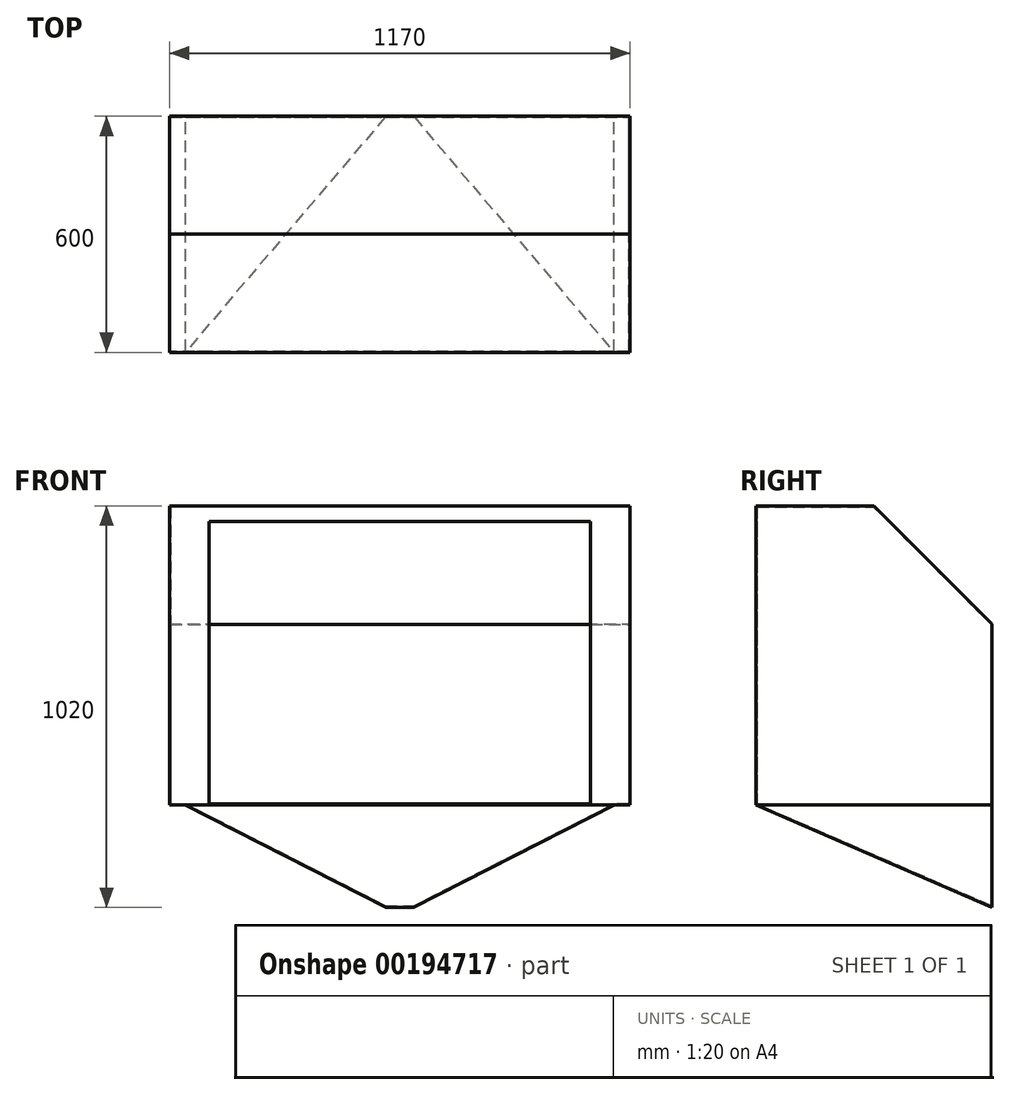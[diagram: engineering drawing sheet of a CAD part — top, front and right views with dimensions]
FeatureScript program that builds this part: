
annotation { "Feature Type Name" : "Feature", "Feature Type Description" : "" }
export const myFeature = defineFeature(function(context is Context, id is Id, definition is map)
    precondition{}
    {
        {
            var Q0;
            Q0=qCreatedBy(makeId("Right.planeOp"),FACE);
            var sketch = newSketch(context, id + "F0", { "sketchPlane" : qUnion([Q0])});
            skLineSegment(sketch, "E0.bottom", {"start": v(-4.06, 760) * mm, "end": v(295.94, 760) * mm});
            skLineSegment(sketch, "E0.top", {"start": v(-4.06, 0) * mm, "end": v(595.94, 0) * mm});
            skLineSegment(sketch, "E0.left", {"start": v(-4.06, 760) * mm, "end": v(-4.06, 0) * mm});
            skLineSegment(sketch, "E0.right", {"start": v(595.94, 460) * mm, "end": v(595.94, 0) * mm});
            skLineSegment(sketch, "E1", {"start": v(295.94, 760) * mm, "end": v(595.94, 460) * mm});
            skLineSegment(sketch, "E2", {"start": v(-4.06, 0) * mm, "end": v(595.94, -260) * mm});
            skLineSegment(sketch, "E3", {"start": v(595.94, -260) * mm, "end": v(595.94, 0) * mm});
            skSolve(sketch);
        }
        {
            var Q0;
            Q0=makeQuery(id+"F0.imprint","IMPRINT",FACE,{"disambiguationData":[TD([[makeQuery(id+"F0.imprint","IMPRINT",EDGE,{"derivedFrom":sQuery(id+"F0.wireOp",EDGE,"E0.bottom")}),-1.0]])]});
            var Q1;
            Q1=makeQuery(id+"F0.imprint","IMPRINT",FACE,{"disambiguationData":[TD([[makeQuery(id+"F0.imprint","IMPRINT",EDGE,{"derivedFrom":sQuery(id+"F0.wireOp",EDGE,"E0.top")}),-1.0]])]});
            extrude(context, id + "F1", {"entities" : qUnion([Q0, Q1]), "oppositeDirection" : true, "depth" : 1170 * mm, "symmetric" : true});
        }
        {
            var Q0;
            {var subQ0=sQuery(id+"F0.wireOp",EDGE,"E3");var subQ2=sQuery(id+"F0.wireOp",EDGE,"E1");var subQ3=sQuery(id+"F0.wireOp",EDGE,"E0.right");Q0=makeQuery(id+"FbMwOEGK0U6XBFF_1.boolean.opBoolean","SPLIT",FACE,{"disambiguationData":[TD([makeQuery(id+"F1.opExtrude","SWEPT_FACE",FACE,{"disambiguationData":[OSD([subQ2])]})])],"derivedFrom":makeQuery(id+"F1.opExtrude","SWEPT_FACE",FACE,{"disambiguationData":[OSD([subQ3,subQ0])]})});}
            var sketch = newSketch(context, id + "F2", { "sketchPlane" : qUnion([Q0])});
            skLineSegment(sketch, "E4", {"start": v(-585, 0) * mm, "end": v(-585, -260) * mm});
            skLineSegment(sketch, "E5", {"start": v(-585, -260) * mm, "end": v(-35, -260) * mm});
            skLineSegment(sketch, "E6", {"start": v(585, -260) * mm, "end": v(585, 0) * mm});
            skLineSegment(sketch, "E7", {"start": v(35, -260) * mm, "end": v(585, -260) * mm});
            skLineSegment(sketch, "E8", {"start": v(-585, 0) * mm, "end": v(-545, 0) * mm});
            skLineSegment(sketch, "E9", {"start": v(-545, 0) * mm, "end": v(-35, -260) * mm});
            skLineSegment(sketch, "E10", {"start": v(585, 0) * mm, "end": v(545, 0) * mm});
            skLineSegment(sketch, "E11", {"start": v(545, 0) * mm, "end": v(35, -260) * mm});
            skSolve(sketch);
        }
        {
            var Q0;
            Q0=makeQuery(id+"F2.imprint","IMPRINT",FACE,{"disambiguationData":[TD([[makeQuery(id+"F2.imprint","IMPRINT",EDGE,{"derivedFrom":sQuery(id+"F2.wireOp",EDGE,"E4")}),1.0]])]});
            var Q1;
            Q1=makeQuery(id+"F2.imprint","IMPRINT",FACE,{"disambiguationData":[TD([[makeQuery(id+"F2.imprint","IMPRINT",EDGE,{"derivedFrom":sQuery(id+"F2.wireOp",EDGE,"E6")}),-1.0]])]});
            extrude(context, id + "F3", {"entities" : qUnion([Q0, Q1]), "operationType" : NewBodyOperationType.REMOVE, "endBound" : BoundingType.THROUGH_ALL, "oppositeDirection" : true, "depth" : 25 * mm});
        }
        {
            var Q0;
            Q0=makeQuery(id+"F1.opExtrude","SWEPT_FACE",FACE,{"disambiguationData":[OSD([sQuery(id+"F0.wireOp",EDGE,"E0.left")])]});
            shell(context, id + "F4", {"entities" : qUnion([Q0]), "thickness" : 2.5 * mm});
        }
        {
            var Q0;
            {var subQ0=makeQuery(id+"F1.opExtrude","SWEPT_FACE",FACE,{"disambiguationData":[OSD([sQuery(id+"F0.wireOp",EDGE,"E0.right")])]});Q0=makeQuery(id+"FFsGgMnDsrMl6fX_1.boolean.opBoolean","MERGE",FACE,{"derivedFrom":[subQ0,makeQuery(id+"F2FXjvtt2T8WuFh_2.opPattern","COPY",FACE,{"derivedFrom":subQ0,"instanceName":"1"}),makeQuery(id+"FFsGgMnDsrMl6fX_1.opExtrude","SWEPT_FACE",FACE,{"disambiguationData":[OSD([sQuery(id+"FZ7NtepqDCPp275_1.wireOp",EDGE,"sU0Ndzhe-5L0x-tQlU-vsOd-fbsLByKIB5Rt")])]})]});}
            var sketch = newSketch(context, id + "F5", { "sketchPlane" : qUnion([Q0])});
            skCircle(sketch, "E12", {"center": v(0, -175) * mm, "radius": 80 * mm});
            skSolve(sketch);
        }
        {
            var Q0;
            Q0=makeQuery(id+"F1.opExtrude","SWEPT_FACE",FACE,{"disambiguationData":[OSD([sQuery(id+"F0.wireOp",EDGE,"E0.left")])]});
            var sketch = newSketch(context, id + "F6", { "sketchPlane" : qUnion([Q0])});
            skLineSegment(sketch, "E13.bottom", {"start": v(-585, 760) * mm, "end": v(585, 760) * mm});
            skLineSegment(sketch, "E13.top", {"start": v(-585, 720) * mm, "end": v(585, 720) * mm});
            skLineSegment(sketch, "E13.left", {"start": v(-585, 760) * mm, "end": v(-585, 720) * mm});
            skLineSegment(sketch, "E13.right", {"start": v(585, 760) * mm, "end": v(585, 720) * mm});
            skLineSegment(sketch, "E14.bottom", {"start": v(585, 760) * mm, "end": v(485, 760) * mm});
            skLineSegment(sketch, "E14.top", {"start": v(585, 0) * mm, "end": v(485, 0) * mm});
            skLineSegment(sketch, "E14.left", {"start": v(585, 760) * mm, "end": v(585, 0) * mm});
            skLineSegment(sketch, "E14.right", {"start": v(485, 760) * mm, "end": v(485, 0) * mm});
            skLineSegment(sketch, "E15.bottom", {"start": v(-585, 760) * mm, "end": v(-485, 760) * mm});
            skLineSegment(sketch, "E15.top", {"start": v(-585, 0) * mm, "end": v(-485, 0) * mm});
            skLineSegment(sketch, "E15.left", {"start": v(-585, 760) * mm, "end": v(-585, 0) * mm});
            skLineSegment(sketch, "E15.right", {"start": v(-485, 760) * mm, "end": v(-485, 0) * mm});
            skSolve(sketch);
        }
        {
            var Q0;
            Q0 = qSketchRegion(id + "F6", true);
            extrude(context, id + "F7", {"entities" : qUnion([Q0]), "operationType" : NewBodyOperationType.ADD, "oppositeDirection" : true, "depth" : 2.5 * mm});
        }
    });
